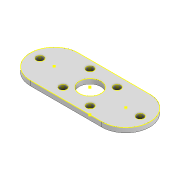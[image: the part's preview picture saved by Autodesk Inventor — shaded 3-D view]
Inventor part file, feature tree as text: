
AUTODESK INVENTOR PART (.ipt)
format: ipt  version: 2022 (Build 260153000, 153)  size: 138,752 bytes
history: native  units: mm
features: extrude x1, sketch x1, projected_geometry x1
ambient origin geometry x8: Origin, YZ Plane, XZ Plane, XY Plane, X Axis, Y Axis, Z Axis, Center Point
bodies: Body1 (feature_tree)
feature tree (3):
  extrude  "Extrusion2"  Depth=20.0mm
  sketch  "Sketch3"  dims[d37=3.0mm d38=3.0mm d39=3.0mm d40=3.0mm d41=9.5mm d42=9.5mm d43=8.0mm d44=8.0mm d55=2.0mm d56=0.0mm d60=20.0mm d61=9.0mm d66=5.0mm d67=5.0mm d68=3.0mm d69=3.0mm d70=6.0mm d71=6.0mm]
  projected_geometry  "Projected Loop1"
